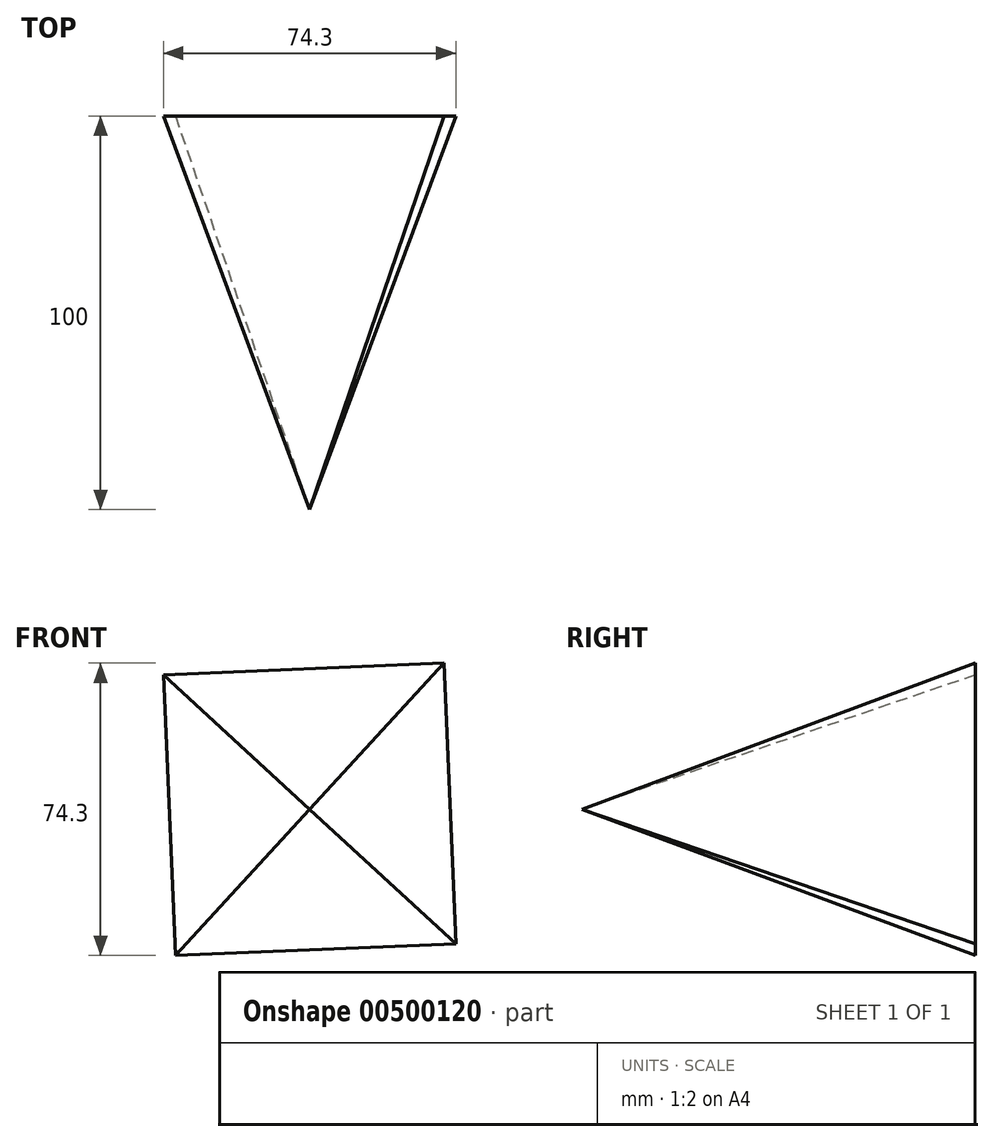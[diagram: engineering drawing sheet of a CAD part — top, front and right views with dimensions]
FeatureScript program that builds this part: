
annotation { "Feature Type Name" : "Feature", "Feature Type Description" : "" }
export const myFeature = defineFeature(function(context is Context, id is Id, definition is map)
    precondition{}
    {
        {
            var Q0;
            Q0=qCreatedBy(makeId("Front.planeOp"),FACE);
            var sketch = newSketch(context, id + "F0", { "sketchPlane" : qUnion([Q0])});
            skCircle(sketch, "E0.cCircle", {"center": v(0, 0) * mm, "radius": 50.46 * mm, "construction": true});
            skLineSegment(sketch, "E0.0", {"start": v(34.14, 37.15) * mm, "end": v(37.15, -34.14) * mm});
            skLineSegment(sketch, "E0.1", {"start": v(37.15, -34.14) * mm, "end": v(-34.14, -37.15) * mm});
            skLineSegment(sketch, "E0.2", {"start": v(-34.14, -37.15) * mm, "end": v(-37.15, 34.14) * mm});
            skLineSegment(sketch, "E0.3", {"start": v(-37.15, 34.14) * mm, "end": v(34.14, 37.15) * mm});
            skSolve(sketch);
        }
        {
            var Q0;
            Q0=qCreatedBy(makeId("Front.planeOp"),FACE);
            cPlane(context, id + "F1", {"entities" : qUnion([Q0]), "cplaneType" : CPlaneType.OFFSET, "offset" : 100 * mm, "width" : 150 * mm, "height" : 150 * mm});
        }
        {
            var Q0;
            Q0=qCreatedBy(id+"F1.planeOp",FACE);
            var sketch = newSketch(context, id + "F2", { "sketchPlane" : qUnion([Q0])});
            skPoint(sketch, "E1", {"position": v(0, 0) * mm});
            skSolve(sketch);
        }
        {
            var Q0;
            Q0=makeQuery(id+"F0.imprint","IMPRINT",FACE,{"disambiguationData":[TD([[makeQuery(id+"F0.imprint","IMPRINT",EDGE,{"derivedFrom":sQuery(id+"F0.wireOp",EDGE,"E0.0")}),-1.0]])]});
            var Q1;
            Q1=sQuery(id+"F2.wireOp",VERTEX,"E1");
            loft(context, id + "F3", {"sheetProfilesArray" : [{ "sheetProfileEntities" : qUnion([Q0]) }, { "sheetProfileEntities" : qUnion([Q1]) }]});
        }
    });
